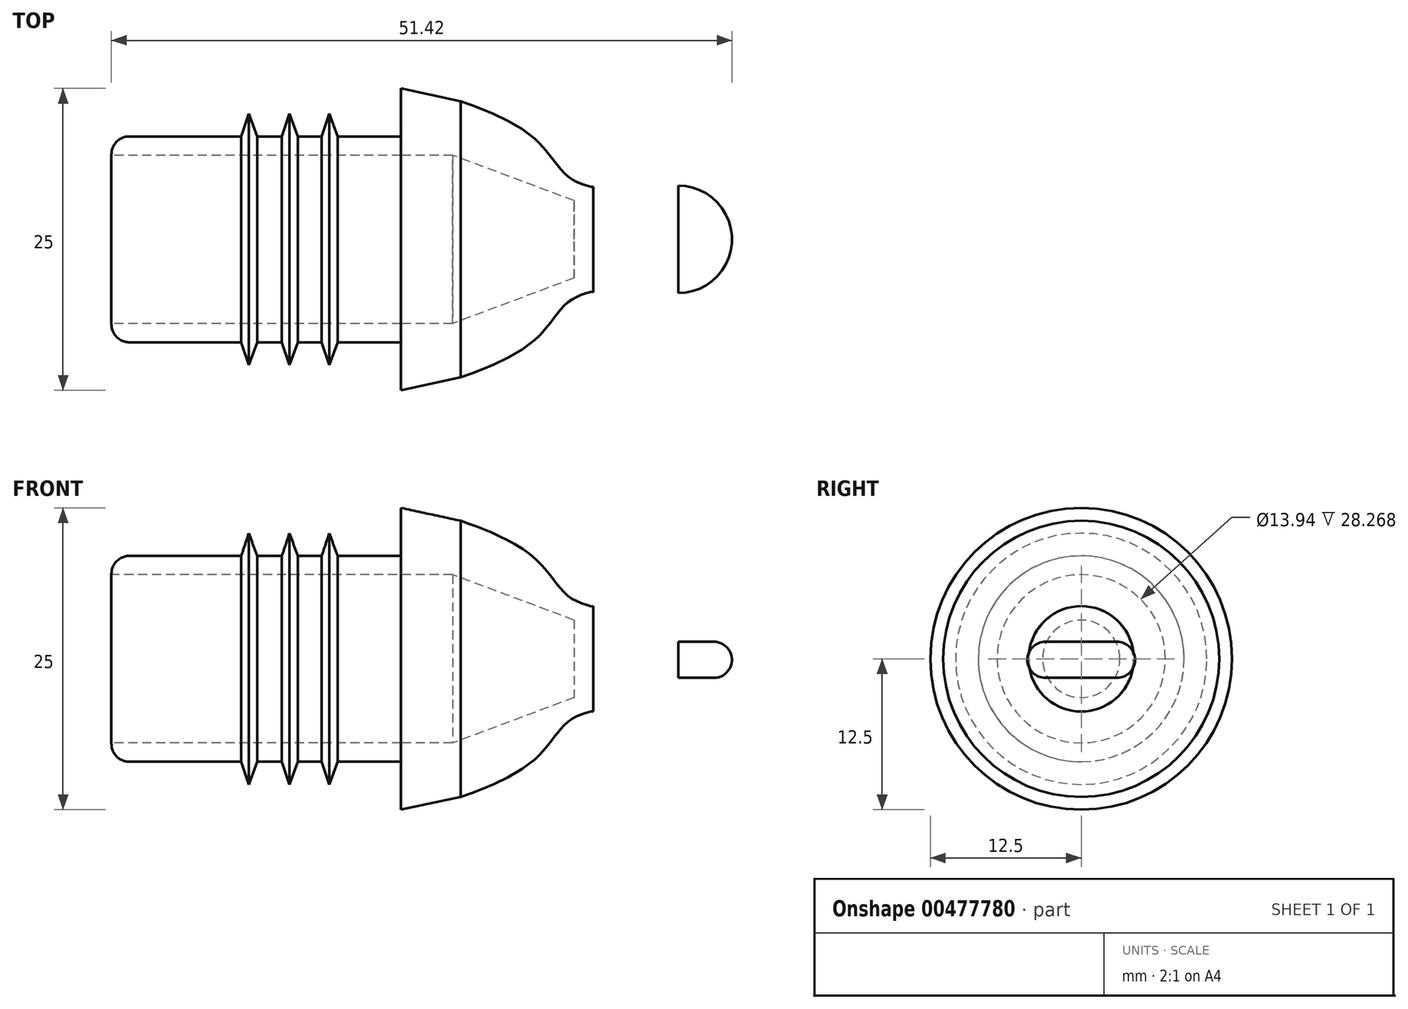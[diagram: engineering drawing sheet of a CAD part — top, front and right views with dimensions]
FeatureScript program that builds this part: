
annotation { "Feature Type Name" : "Feature", "Feature Type Description" : "" }
export const myFeature = defineFeature(function(context is Context, id is Id, definition is map)
    precondition{}
    {
        {
            var Q0;
            Q0=qCreatedBy(makeId("Front.planeOp"),FACE);
            var sketch = newSketch(context, id + "F0", { "sketchPlane" : qUnion([Q0])});
            skLineSegment(sketch, "E0.top", {"start": v(0, 8.53) * mm, "end": v(-24, 8.53) * mm});
            skLineSegment(sketch, "E1", {"start": v(-6.58, 8.53) * mm, "end": v(-5.95, 10.41) * mm});
            skLineSegment(sketch, "E2", {"start": v(-5.95, 10.41) * mm, "end": v(-5.26, 8.53) * mm});
            skLineSegment(sketch, "E3", {"start": v(-9.88, 8.53) * mm, "end": v(-9.25, 10.41) * mm});
            skLineSegment(sketch, "E4", {"start": v(-9.25, 10.41) * mm, "end": v(-8.56, 8.53) * mm});
            skLineSegment(sketch, "E5", {"start": v(-13.25, 8.53) * mm, "end": v(-12.61, 10.41) * mm});
            skLineSegment(sketch, "E6", {"start": v(-12.61, 10.41) * mm, "end": v(-11.93, 8.53) * mm});
            skLineSegment(sketch, "E7", {"start": v(4.95, 11.44) * mm, "end": v(0, 12.5) * mm});
            skFitSpline(sketch, "E8", {"points": [v(4.95, 11.44) * mm, v(8.04, 10.22) * mm, v(11.13, 8.29) * mm, v(12.9, 6.2) * mm, v(13.97, 5.1) * mm, v(15.22, 4.5) * mm, v(15.92, 4.35) * mm, v(15.92, 4.43) * mm], "startDerivative": vector(15.14, -5.41) * mm, "endDerivative": vector(-0.81, 2.96) * mm});
            skLineSegment(sketch, "E9", {"start": v(15.92, 4.4) * mm, "end": v(15.92, 0) * mm});
            skLineSegment(sketch, "E10", {"start": v(15.92, 0) * mm, "end": v(14.35, 0) * mm});
            skLineSegment(sketch, "E11", {"start": v(14.35, 0) * mm, "end": v(14.35, 3.2) * mm});
            skLineSegment(sketch, "E12", {"start": v(-26.85, 0) * mm, "end": v(19.07, 0) * mm});
            skLineSegment(sketch, "E13", {"start": v(0, 12.5) * mm, "end": v(0, 8.53) * mm});
            skLineSegment(sketch, "E14", {"start": v(-24, 8.53) * mm, "end": v(-24, 6.97) * mm});
            skLineSegment(sketch, "E15", {"start": v(-24, 6.97) * mm, "end": v(4.27, 6.97) * mm});
            skLineSegment(sketch, "E16", {"start": v(4.27, 6.97) * mm, "end": v(14.35, 3.2) * mm});
            skSolve(sketch);
        }
        {
            var Q0;
            {var subQ0=sQuery(id+"F0.wireOp",EDGE,"E1");Q0=makeQuery(id+"F0.imprint","IMPRINT",FACE,{"disambiguationData":[TD([[makeQuery(id+"F0.imprint","IMPRINT",EDGE,{"derivedFrom":subQ0}),-1.0]])]});}
            var Q1;
            Q1=makeQuery(id+"F0.imprint","IMPRINT",FACE,{"disambiguationData":[TD([[makeQuery(id+"F0.imprint","IMPRINT",EDGE,{"derivedFrom":sQuery(id+"F0.wireOp",EDGE,"E7")}),1.0]])]});
            var Q2;
            {var subQ0=sQuery(id+"F0.wireOp",EDGE,"E3");Q2=makeQuery(id+"F0.imprint","IMPRINT",FACE,{"disambiguationData":[TD([[makeQuery(id+"F0.imprint","IMPRINT",EDGE,{"derivedFrom":subQ0}),-1.0]])]});}
            var Q3;
            {var subQ0=sQuery(id+"F0.wireOp",EDGE,"E5");Q3=makeQuery(id+"F0.imprint","IMPRINT",FACE,{"disambiguationData":[TD([[makeQuery(id+"F0.imprint","IMPRINT",EDGE,{"derivedFrom":subQ0}),-1.0]])]});}
            var Q4;
            Q4=sQuery(id+"F0.wireOp",EDGE,"E12");
            revolve(context, id + "F1", {"entities" : qUnion([Q0, Q1, Q2, Q3]), "axis" : qUnion([Q4]), "revolveType" : RevolveType.FULL});
        }
        {
            var Q0;
            Q0=qCreatedBy(makeId("Front.planeOp"),FACE);
            var sketch = newSketch(context, id + "F2", { "sketchPlane" : qUnion([Q0])});
            skLineSegment(sketch, "E17.right", {"start": v(22.96, -1.58) * mm, "end": v(22.96, 1.42) * mm});
            skArc(sketch, "E18", {"start": v(25.92, -1.58) * mm, "mid": v(27.42, -0.08) * mm, "end": v(25.92, 1.42) * mm});
            skLineSegment(sketch, "E19", {"start": v(22.96, 1.42) * mm, "end": v(25.92, 1.42) * mm});
            skLineSegment(sketch, "E20", {"start": v(22.96, -1.58) * mm, "end": v(25.92, -1.58) * mm});
            skSolve(sketch);
        }
        {
            var Q0;
            Q0=makeQuery(id+"F2.imprint","IMPRINT",FACE,{"disambiguationData":[TD([[makeQuery(id+"F2.imprint","IMPRINT",EDGE,{"derivedFrom":sQuery(id+"F2.wireOp",EDGE,"E17.right")}),-1.0]])]});
            var Q1;
            Q1=sQuery(id+"F2.wireOp",EDGE,"E17.right");
            revolve(context, id + "F3", {"entities" : qUnion([Q0]), "axis" : qUnion([Q1]), "revolveType" : RevolveType.SYMMETRIC, "angle" : 180 * degree});
        }
        {
            var Q0;
            Q0=makeQuery(id+"F1.opRevolve","SWEPT_FACE",FACE,{"disambiguationData":[OSD([sQuery(id+"F0.wireOp",EDGE,"E9")])]});
            var Q1;
            Q1=makeQuery(id+"F3.opRevolve","CAP_FACE",FACE,{"disambiguationData":[OSD([sQuery(id+"F2.wireOp",EDGE,"E17.right"),sQuery(id+"F2.wireOp",EDGE,"E18"),sQuery(id+"F2.wireOp",EDGE,"E19"),sQuery(id+"F2.wireOp",EDGE,"E20")])],"isStart":false});
            loft(context, id + "F4", {"bodyType" : ToolBodyType.SURFACE, "endCondition" : LoftEndDerivativeType.NORMAL_TO_PROFILE, "endMagnitude" : 1, "wireProfilesArray" : [{ "wireProfileEntities" : qUnion([Q0]) }, { "wireProfileEntities" : qUnion([Q1]) }]});
        }
        {
            var Q0;
            Q0=makeQuery(id+"F1.opRevolve","SWEPT_EDGE",EDGE,{"disambiguationData":[OSD([sQuery(id+"F0.wireOp",EDGE,"E0.top"),sQuery(id+"F0.wireOp",EDGE,"E14")])]});
            fillet(context, id + "F5", {"entities" : qUnion([Q0]), "radius" : 1.5 * mm, "tangentPropagation" : true, "allowEdgeOverflow" : false});
        }
    });
